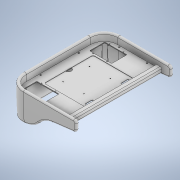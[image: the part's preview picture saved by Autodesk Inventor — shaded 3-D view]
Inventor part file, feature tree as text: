
AUTODESK INVENTOR PART (.ipt)
format: ipt  version: 2021 (Build 250183000, 183)  size: 1,779,200 bytes
history: native  units: mm
features: sketch x22, projected_geometry x13, extrude x11, fillet x7, hole x7, mirror x6, other x6, plane x5, loft x1, chamfer x1
ambient origin geometry x8: Origin, YZ Plane, XZ Plane, XY Plane, X Axis, Y Axis, Z Axis, Center Point
bodies: Body1 (feature_tree), Body2 (feature_tree), Body3 (feature_tree), Body4 (feature_tree)
feature tree (79):
  sketch  "草圖1"
  plane  "工作平面1"
  sketch  "草圖2"
  plane  "工作平面2"
  sketch  "草圖3"
  sketch  "草圖5"
  plane  "工作平面4"
  loft  "斷面混成3"
  plane  "工作平面3"
  extrude  "擠出2"  Depth=700.0mm
  fillet  "圓角8"  Radius=500.0mm
  fillet  "圓角9"  Radius=20.0mm
  fillet  "圓角10"  Radius=20.0mm
  plane  "工作平面5"
  chamfer  "倒角2"  Distance=100.0mm
  hole  "孔1"  [1 undecoded]
  extrude  "擠出3"  [1 undecoded]
  hole  "孔2"  [1 undecoded]
  extrude  "擠出4"  [1 undecoded]
  fillet  "圓角12"  [1 undecoded]
  extrude  "擠出6"  [1 undecoded]
  mirror  "鏡射1"
  hole  "孔3"  [1 undecoded]
  extrude  "擠出7"  TaperAngle=0.0deg  [1 undecoded]
  hole  "孔4"  [1 undecoded]
  fillet  "圓角13"  Radius=75.0mm
  mirror  "鏡射2"
  extrude  "擠出8"  Depth=10.0mm
  mirror  "鏡射3"
  sketch  "草圖24"
  extrude  "擠出15"  Depth=325.0mm
  hole  "孔5"  [1 undecoded]
  mirror  "鏡射4"
  extrude  "擠出18"  Depth=150.0mm
  fillet  "圓角18"  Radius=20.0mm
  extrude  "擠出17"  [1 undecoded]
  fillet  "圓角17"  Radius=20.0mm
  extrude  "擠出19"  Depth=85.451367mm
  extrude  "擠出20"  Depth=12.0mm TaperAngle=45.0deg
  mirror  "鏡射5"
  hole  "孔6"  [1 undecoded]
  hole  "孔7"  [1 undecoded]
  mirror  "鏡射6"
  sketch  "草圖6"
  other  "實體3"
  sketch  "草圖7"
  sketch  "草圖8"
  sketch  "草圖9"
  projected_geometry  "投影迴路1"
  sketch  "草圖10"
  projected_geometry  "投影迴路2"
  other  "實體4"
  sketch  "草圖11"
  projected_geometry  "投影迴路3"
  projected_geometry  "投影迴路4"
  projected_geometry  "投影迴路5"
  projected_geometry  "投影迴路6"
  projected_geometry  "投影迴路7"
  projected_geometry  "投影迴路8"
  sketch  "草圖12"
  other  "實體5"
  projected_geometry  "投影迴路10"
  sketch  "草圖15"
  sketch  "草圖16"
  sketch  "草圖17"
  sketch  "草圖18"
  projected_geometry  "投影迴路11"
  sketch  "草圖26"
  projected_geometry  "投影迴路17"
  sketch  "草圖27"
  projected_geometry  "投影迴路18"
  other  "實體7"
  sketch  "草圖28"
  sketch  "草圖29"
  projected_geometry  "投影迴路19"
  sketch  "草圖30"
  sketch  "草圖31"
  other  "投影切割邊1"
  other  "投影切割邊2"
note: 13 required parameter values undecoded (feature->parameter linkage not recoverable at this tier; creation-order binding heuristic only, values carry confidence <= 0.55)
